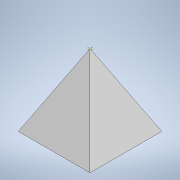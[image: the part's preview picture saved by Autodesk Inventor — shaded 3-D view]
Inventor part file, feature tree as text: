
AUTODESK INVENTOR PART (.ipt)
format: ipt  version: 2020 (Build 240168000, 168)  size: 122,368 bytes
history: native  units: in
note: dims shown in document units (in); Inventor stores cm internally (conversion verified against a paired STEP export)
features: sketch x6, extrude x5, plane x4
ambient origin geometry x8: Origin, YZ Plane, XZ Plane, XY Plane, X Axis, Y Axis, Z Axis, Center Point
bodies: Solid1 (feature_tree)
feature tree (15):
  extrude  "Extrusion1"  Depth=0.5906in
  sketch  "Sketch2"  dims[d2=0.5906in d3=0.0in]
  plane  "Work Plane1"
  plane  "Work Plane2"
  plane  "Work Plane3"
  plane  "Work Plane4"
  extrude  "Extrusion2"  TaperAngle=0.0deg  [1 undecoded]
  extrude  "Extrusion3"  Depth=0.1033in TaperAngle=0.0deg
  extrude  "Extrusion4"  TaperAngle=0.0deg  [1 undecoded]
  extrude  "Extrusion5"  [1 undecoded]
  sketch  "Sketch1"  dims[d0=0.5906in d1=0.5906in]
  sketch  "Sketch4"  dims[d4=0.1264in d5=0.0in d6=0.1033in d7=0.0in]
  sketch  "Sketch5"  dims[d8=0.5906in d9=0.0in]
  sketch  "Sketch6"  dims[d10=0.0508in d11=0.0in]
  sketch  "Sketch7"
note: 3 required parameter values undecoded (feature->parameter linkage not recoverable at this tier; creation-order binding heuristic only, values carry confidence <= 0.55)
